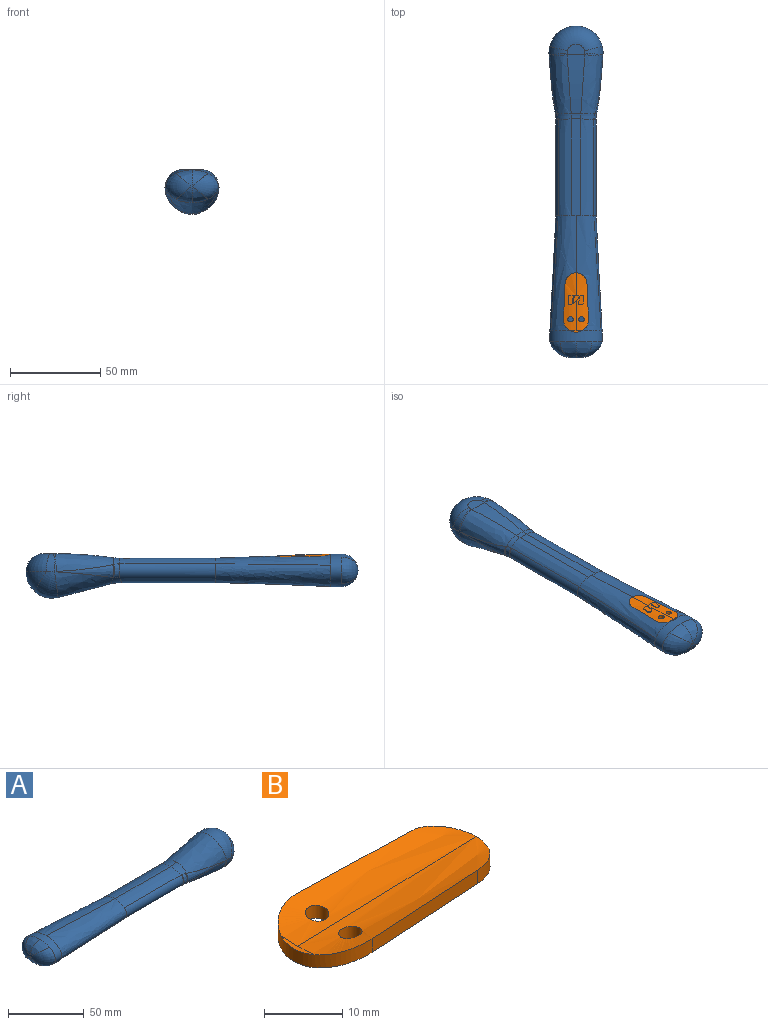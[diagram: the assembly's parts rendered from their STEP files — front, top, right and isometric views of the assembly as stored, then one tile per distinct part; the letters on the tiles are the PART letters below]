
ASSEMBLY  parts=2 mates=1
PART A: 106 faces, bbox 187.8x34.4x30.2 mm
  f0: bspline ~63.85x22.85mm, area 654.6mm2, adj f1,f11,f13,f26,f27,f51,f52,f54
  f1: bspline ~63.85x22.85mm, area 654.6mm2, adj f0,f11,f27,f35,f47,f52,f53,f54
  f2: plane 9.95x5.98mm, normal (0,0,-1), area 48.9mm2, adj f6,f8,f9,f10,f32,f33
  f3: sphere r=15mm, area 530.8mm2, adj f5,f10
  f4: bspline ~35x30mm, area 1066.7mm2, adj f5,f14,f22,f23,f36,f43,f44
  f5: bspline ~30.36x18.63mm, area 488mm2, adj f3,f4,f24,f25,f45,f46
  f6: cylinder r=234.57mm len=32.66mm, axis (0,-1,0), area 248.2mm2, adj f2,f7,f16,f17,f31,f38
  f7: bspline ~32.81x12.21mm, area 426.1mm2, adj f6,f8,f15,f21,f22
  f8: cylinder r=10mm len=10.04mm, axis (1,0.07,0), area 13.6mm2, adj f2,f7,f9,f23,f24
  f9: bspline ~10.48x10mm, area 53.7mm2, adj f2,f8,f10,f25
  f10: torus R=5mm, axis (0,0,1), area 471mm2, adj f2,f3,f9,f33
  f11: plane 53.75x5.33mm, normal (0,0,-1), area 276.2mm2, adj f0,f1,f13,f17,f35
  f12: extruded ~52.96x8.91mm, area 495.5mm2, adj f14,f18,f26,f34
  f13: extruded ~53.57x7.21mm, area 431.2mm2, adj f0,f11,f15,f16,f18,f19
  f14: bspline ~12.64x5.98mm, area 53mm2, adj f4,f12,f19,f20,f21,f36
  f15: bspline ~8.11x4.23mm, area 25.4mm2, adj f7,f13,f16,f20
  f16: bspline ~3.26x2.79mm, area 0.2mm2, adj f6,f13,f15,f17
  f17: cylinder r=20mm len=5.16mm, axis (0,-1,0), area 14.4mm2, adj f6,f11,f16,f38
  f18: cylinder r=5.08mm len=52.96mm, axis (1,0,0), area 467.3mm2, adj f12,f13,f19,f26
  f19: bspline ~7.75x5.06mm, area 4.3mm2, adj f13,f14,f18,f20
  f20: bspline ~7.73x5.09mm, area 23.7mm2, adj f14,f15,f19,f21
  f21: bspline ~7.36x4.23mm, area 3.9mm2, adj f7,f14,f20,f22
  f22: bspline ~34.5x7.33mm, area 102.2mm2, adj f4,f7,f21,f23
  f23: bspline ~4.97x0.54mm, area 0.1mm2, adj f4,f8,f22,f24
  f24: bspline ~0.13x0.1mm, area 0mm2, adj f5,f8,f23,f25
  f25: bspline ~4.65x0.45mm, area 0.1mm2, adj f5,f9,f24
  f26: bspline ~65.13x22.09mm, area 1290.3mm2, adj f0,f12,f18,f27,f47
  f27: extruded ~29x18mm, area 449.1mm2, adj f0,f1,f26,f28,f29,f30,f47,f48
  f28: bspline ~10.06x9.81mm, area 56.2mm2, adj f27,f30,f48
  f29: bspline ~10.1x10.06mm, area 56.4mm2, adj f27,f30,f49
  f30: bspline ~14.5x14.3mm, area 128.7mm2, adj f27,f28,f29
  f31: bspline ~32.81x12.21mm, area 426.1mm2, adj f6,f32,f37,f42,f43
  f32: cylinder r=10mm len=10.04mm, axis (1,-0.07,0), area 13.6mm2, adj f2,f31,f33,f44,f45
  f33: bspline ~10.48x10mm, area 53.7mm2, adj f2,f10,f32,f46
  f34: extruded ~52.96x8.91mm, area 495.5mm2, adj f12,f36,f39,f47
  f35: extruded ~53.57x7.21mm, area 431.2mm2, adj f1,f11,f37,f38,f39,f40
  f36: bspline ~12.64x5.98mm, area 53mm2, adj f4,f14,f34,f40,f41,f42
  f37: bspline ~8.11x4.23mm, area 25.4mm2, adj f31,f35,f38,f41
  f38: bspline ~3.26x2.79mm, area 0.2mm2, adj f6,f17,f35,f37
  f39: cylinder r=5.08mm len=52.96mm, axis (1,0,0), area 467.3mm2, adj f34,f35,f40,f47
  f40: bspline ~7.75x5.06mm, area 4.3mm2, adj f35,f36,f39,f41
  f41: bspline ~7.73x5.09mm, area 23.7mm2, adj f36,f37,f40,f42
  f42: bspline ~7.36x4.23mm, area 3.9mm2, adj f31,f36,f41,f43
  f43: bspline ~34.12x7.23mm, area 102.2mm2, adj f4,f31,f42,f44
  f44: bspline ~4.97x0.54mm, area 0.1mm2, adj f4,f32,f43,f45
  f45: bspline ~0.13x0.1mm, area 0mm2, adj f5,f32,f44,f46
  f46: bspline ~4.65x0.45mm, area 0.1mm2, adj f5,f33,f45
  f47: bspline ~65.13x22.09mm, area 1290.3mm2, adj f1,f26,f27,f34,f39
  f48: bspline ~10.06x9.81mm, area 56.2mm2, adj f27,f28,f50
  f49: bspline ~10.1x10.06mm, area 56.4mm2, adj f27,f29,f50
  f50: bspline ~14.5x14.3mm, area 119.2mm2, adj f27,f48,f49
  f51: plane 19.88x2.49mm, normal (-0.04,-1,0), area 42.2mm2, adj f0,f52,f54,f105
  f52: cylinder r=6.08mm len=12.15mm, axis (0,0,1), area 38.2mm2, adj f0,f1,f51,f53,f104,f105
  f53: plane 19.88x2.49mm, normal (-0.04,1,0), area 42.2mm2, adj f1,f52,f54,f104
  f54: cylinder r=6.93mm len=13.86mm, axis (0,0,1), area 46.1mm2, adj f0,f1,f27,f51,f53,f103,f104,f105
  f55: bspline ~4x0.39mm, area 0.1mm2, adj f61,f62,f64
  f56: sphere r=13mm, area 257.6mm2, adj f60,f64
  f57: bspline ~4x0.39mm, area 0.1mm2, adj f58,f59,f64
  f58: bspline ~0.12x0.06mm, area 0mm2, adj f57,f64,f65,f67
  f59: bspline ~8.48x8mm, area 37.8mm2, adj f57,f60,f67,f68
  f60: torus R=5mm, axis (0,0,1), area 334.6mm2, adj f56,f59,f61,f68
  f61: bspline ~8.48x8mm, area 37.8mm2, adj f55,f60,f68,f69
  f62: bspline ~0.12x0.06mm, area 0mm2, adj f55,f63,f64,f69
  f63: bspline ~4.97x0.37mm, area 0.1mm2, adj f62,f69,f70,f72
  f64: bspline ~26.3x16.09mm, area 362.6mm2, adj f55,f56,f57,f58,f62,f72
  f65: bspline ~4.97x0.37mm, area 0.1mm2, adj f58,f66,f67,f72
  f66: bspline ~33.22x4.78mm, area 61.2mm2, adj f65,f72,f73,f75
  f67: cylinder r=8mm len=8.04mm, axis (1,0.07,0), area 10.9mm2, adj f58,f59,f65,f68,f75
  f68: plane 9.95x5.98mm, normal (0,0,1), area 48.9mm2, adj f59,f60,f61,f67,f69,f76
  f69: cylinder r=8mm len=8.04mm, axis (1,-0.07,0), area 10.9mm2, adj f61,f62,f63,f68,f77
  f70: bspline ~33.64x4.74mm, area 61.2mm2, adj f63,f71,f72,f77
  f71: bspline ~4.46x3.01mm, area 2.4mm2, adj f70,f77,f78,f79
  f72: offset ~39x34mm, area 921.1mm2, adj f63,f64,f65,f66,f70,f79,f80
  f73: bspline ~4.46x3.01mm, area 2.4mm2, adj f66,f74,f75,f80
  f74: bspline ~5.49x4.69mm, area 16mm2, adj f73,f80,f81,f82
  f75: bspline ~32.5x10.21mm, area 338.8mm2, adj f66,f67,f73,f76,f82
  f76: cylinder r=232.57mm len=32.38mm, axis (0,-1,0), area 246.1mm2, adj f68,f75,f77,f83,f84,f85
  f77: bspline ~32.5x10.21mm, area 338.8mm2, adj f69,f70,f71,f76,f86
  f78: bspline ~5.49x4.69mm, area 16mm2, adj f71,f79,f86,f87
  f79: bspline ~8.6x6.48mm, area 50.2mm2, adj f71,f72,f78,f80,f87,f89
  f80: bspline ~8.6x6.48mm, area 50.2mm2, adj f72,f73,f74,f79,f81,f90
  f81: bspline ~4.7x3.07mm, area 2.7mm2, adj f74,f80,f91,f92
  f82: bspline ~6.5x3.43mm, area 22.3mm2, adj f74,f75,f83,f92
  f83: bspline ~3.25x3.07mm, area 0.2mm2, adj f76,f82,f84,f92
  f84: cylinder r=22mm len=5.16mm, axis (0,-1,0), area 15.8mm2, adj f76,f83,f85,f93
  f85: bspline ~3.26x3.07mm, area 0.2mm2, adj f76,f84,f86,f94
  f86: bspline ~6.5x3.43mm, area 22.3mm2, adj f77,f78,f85,f94
  f87: bspline ~4.7x3.07mm, area 2.7mm2, adj f78,f79,f88,f94
  f88: cylinder r=3.08mm len=53.02mm, axis (1,0,0), area 283.6mm2, adj f87,f89,f94,f95
  f89: extruded ~53.01x7.8mm, area 434.1mm2, adj f79,f88,f90,f95
  f90: extruded ~53.01x7.8mm, area 434mm2, adj f80,f89,f91,f96
  f91: cylinder r=3.08mm len=53.02mm, axis (1,0,0), area 283.5mm2, adj f81,f90,f92,f96
  f92: extruded ~53.63x5.75mm, area 344.3mm2, adj f81,f82,f83,f91,f93,f105
  f93: plane 53.79x5.34mm, normal (0,0,1), area 276.4mm2, adj f84,f92,f94,f104,f105
  f94: extruded ~53.63x5.75mm, area 344.3mm2, adj f85,f86,f87,f88,f93,f104
  f95: offset ~69.13x26.09mm, area 992.1mm2, adj f88,f89,f96,f103,f104
  f96: offset ~69.13x26.09mm, area 991.7mm2, adj f90,f91,f95,f103,f105
  f97: bspline ~10.24x8.11mm, area 40.3mm2, adj f98,f102,f103
  f98: offset ~18.5x18.3mm, area 117.5mm2, adj f97,f99,f103
  f99: bspline ~8.95x8.08mm, area 40.2mm2, adj f98,f100,f103
  f100: bspline ~8.95x8.08mm, area 40.2mm2, adj f99,f101,f103
  f101: offset ~18.5x18.3mm, area 117.5mm2, adj f100,f102,f103
  f102: bspline ~10.24x8.11mm, area 40.3mm2, adj f97,f101,f103
  f103: extruded ~24.96x13.96mm, area 370.9mm2, adj f54,f95,f96,f97,f98,f99,f100,f101
  f104: offset ~68.63x22.67mm, area 529.4mm2, adj f52,f53,f54,f93,f94,f95,f103,f105
  f105: offset ~68.63x22.67mm, area 529.6mm2, adj f51,f52,f54,f92,f93,f96,f103,f104
PART B: 28 faces, bbox 69.3x23.1x7.8 mm
  f0: plane 8.85x5.19mm, normal (0,0,-1), area 30.8mm2, adj f1,f2,f3,f4,f5,f6,f7,f8
  f1: extruded ~1.16x0.82mm, area 0.6mm2, adj f0,f2,f15,f19
  f2: plane 2.56x0.46mm, normal (0.15,-0.99,0), area 1mm2, adj f0,f1,f3,f19
  f3: extruded ~2.78x1.39mm, area 1.9mm2, adj f0,f2,f4,f19
  f4: plane 3.07x0.78mm, normal (-0.13,0.99,0), area 2.1mm2, adj f0,f3,f5,f19
  f5: extruded ~2.98x1.1mm, area 2.5mm2, adj f0,f4,f6,f19
  f6: plane 0.98x0.47mm, normal (-0.11,0.99,0), area 0.4mm2, adj f0,f5,f7,f19
  f7: plane 2.77x0.48mm, normal (1,-0.05,0), area 1.2mm2, adj f0,f6,f8,f18,f19
  f8: plane 0.45x0.2mm, normal (-0.75,-0.66,0), area 0.1mm2, adj f0,f7,f9,f18
  f9: extruded ~3.77x0.94mm, area 1.6mm2, adj f0,f8,f10,f18
  f10: plane 4.01x0.5mm, normal (-0.12,0.99,0), area 1.7mm2, adj f0,f9,f11,f18
  f11: plane 2.77x0.78mm, normal (1,-0.05,0), area 1.6mm2, adj f0,f10,f12,f18
  f12: plane 0.77x0.25mm, normal (-0.78,-0.63,0), area 0.2mm2, adj f0,f11,f13,f18
  f13: plane 3.35x0.72mm, normal (0.13,-0.99,0), area 2.4mm2, adj f0,f12,f14,f18
  f14: extruded ~2.82x1.34mm, area 2mm2, adj f0,f13,f15,f18
  f15: plane 2.37x2.24mm, normal (-0.73,0.69,0), area 1.1mm2, adj f0,f1,f14,f18,f19
  f16: cylinder r=1.5mm len=3mm, axis (0,0,1), area 19mm2, adj f19,f23
  f17: extruded ~6.33x0.77mm, area 3.3mm2, adj f18,f19,f25
  f18: bspline ~64.49x15.43mm, area 174.7mm2, adj f7,f8,f9,f10,f11,f12,f13,f14
  f19: bspline ~64.49x15.43mm, area 175.5mm2, adj f1,f2,f3,f4,f5,f6,f7,f15
  f20: cylinder r=1.5mm len=3mm, axis (0,0,1), area 19mm2, adj f18,f21
  f21: offset ~69.13x19.43mm, area 191mm2, adj f20,f22,f23,f25,f26,f27
  f22: extruded ~6.21x0.73mm, area 3.1mm2, adj f21,f23,f25
  f23: offset ~69.13x19.43mm, area 191.1mm2, adj f16,f21,f22,f24,f25,f26
  f24: plane 19.88x2.49mm, normal (0.04,1,0), area 42.2mm2, adj f19,f23,f25,f26
  f25: cylinder r=6.93mm len=13.86mm, axis (0,0,-1), area 46.1mm2, adj f17,f18,f19,f21,f22,f23,f24,f27
  f26: cylinder r=6.08mm len=12.15mm, axis (0,0,-1), area 38.2mm2, adj f18,f19,f21,f23,f24,f27
  f27: plane 19.88x2.49mm, normal (0.04,-1,0), area 42.2mm2, adj f18,f21,f25,f26
PLACE A rot(axis=(-0.71,-0.71,0),180deg) t=(-12.75,125.84,-35.82)mm
PLACE B rot(axis=(-0.71,-0.71,0),180deg) t=(-12.75,125.84,-35.82)mm
MATE fastened B.f24 <-> A.f51  axis (1,0.04,0) through (-6.25,-26.63,-28.62)mm
